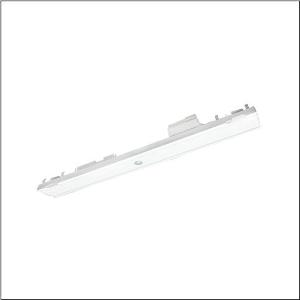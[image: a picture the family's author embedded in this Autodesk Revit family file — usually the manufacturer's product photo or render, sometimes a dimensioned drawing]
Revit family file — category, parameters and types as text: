
# Revit family: licross_r_56tl157c4x31_efa4
name_source: partatom
category: Lighting Fixtures
units: mm (PartAtom-declared; Revit-internal decimal feet)

## family parameters
Cut with Voids When Loaded = No
Host = Face
Light Source = No
Part Type = Normal
Room Calculation Point = No
Round Connector Dimension = Use Diameter
Shared = No

## types (1)
- Licross® (1 x LED, 320 lm, 3.9 W, 4000K)
    Apparent Load = 4 VA
    CIE Flux Codes = 31 68 99 100 100
    Color Rendering = 70
    Color Temperature = 4000K
    Default Elevation = 1800 mm
    Description = Licross®, luminaire insert, of sheet steel, coil coated, white, length: 500mm, width: 59mm, height: 60mm, mounting height: 2.5..7m, emergency light element,LED rated luminous flux: 320lm, light colour: 740, control gear: CEAG, with plug, 6-pole, with phase selection, mains connection: 220..240V, AC/DC, 0/50..60Hz, rated input power: 3.9W, halogen-free wiring, for trunking rail, 9..14-pole, for emergency light function, supply monitoring module CEAG, with address switch, choice between two emergency light lines via tool-free moving of contact pin prior to installation in trunking rail, primary light control with lens, of PMMA, primary optical cover: cover, of PMMA, light emission: direct distribution, primary light characteristic: symmetric,  for area, compatible with all CEAG STAR technology systems (ZB-S, DG-S (DualGuard-S), LP-STAR, AT-S+), protection rating (complete): IP40, insulation class (complete): insulation class I (protective earthing), certification: CE, UKCA, protection symbol: D if used in an environment without relevant dust loads, impact resistance: IK06, permissible ambient temperature for indoor applications: -20..+40°C, packaging unit: 1 piece
    Height = 60 mm  [stored 0.19685 ft]
    Lamp = 1 x LED
    Lamp Light Flux = 320 lm
    Lamp Power = 3.9 W
    Lamp count = 1
    Length = 500 mm
    Luminous efficacy = 82 lm/W
    Manufacturer = Siteco
    ModVariant = No
    Model = 56TL157C4X31
    Mounting Place = Ceiling
    Mounting Type = Pendant
    Number of Poles = 1
    OnlyDefault = Yes
    Power Factor = 1
    Product Name = Licross®
    Product group = luminaire insert
    ProductGroupID = 901
    Protection Class = Protection class I
    Protection Degree = IP 40
    RLX_Detail_Level = 1
    RLX_Emergency_Light_Flux = 0 lm
    RLX_Emergency_Type = 0
    RLX_Emergency_Type_DB = No
    RlxData = <blob elided: 27913 chars, md5=95e8ccf5>
    Socket = socket
    Standby Power = 0 W
    System Light Flux = 320 lm
    System Power = 4 W
    Type Comments = Product without accessories
    Type Image = l_1251804.jpg
    URL = http://relux.com
    VarID = ---
    Voltage = 0 V
    Weight = 0.00 kg
    Width = 59 mm

note: [stored X ft] marks values corroborated as IEEE doubles in the binary element streams (Revit-internal decimal feet)

## geometry (parser evidence)
native form markers: Blend x4, Sweep x11
no freeform markers — native parametric forms only
